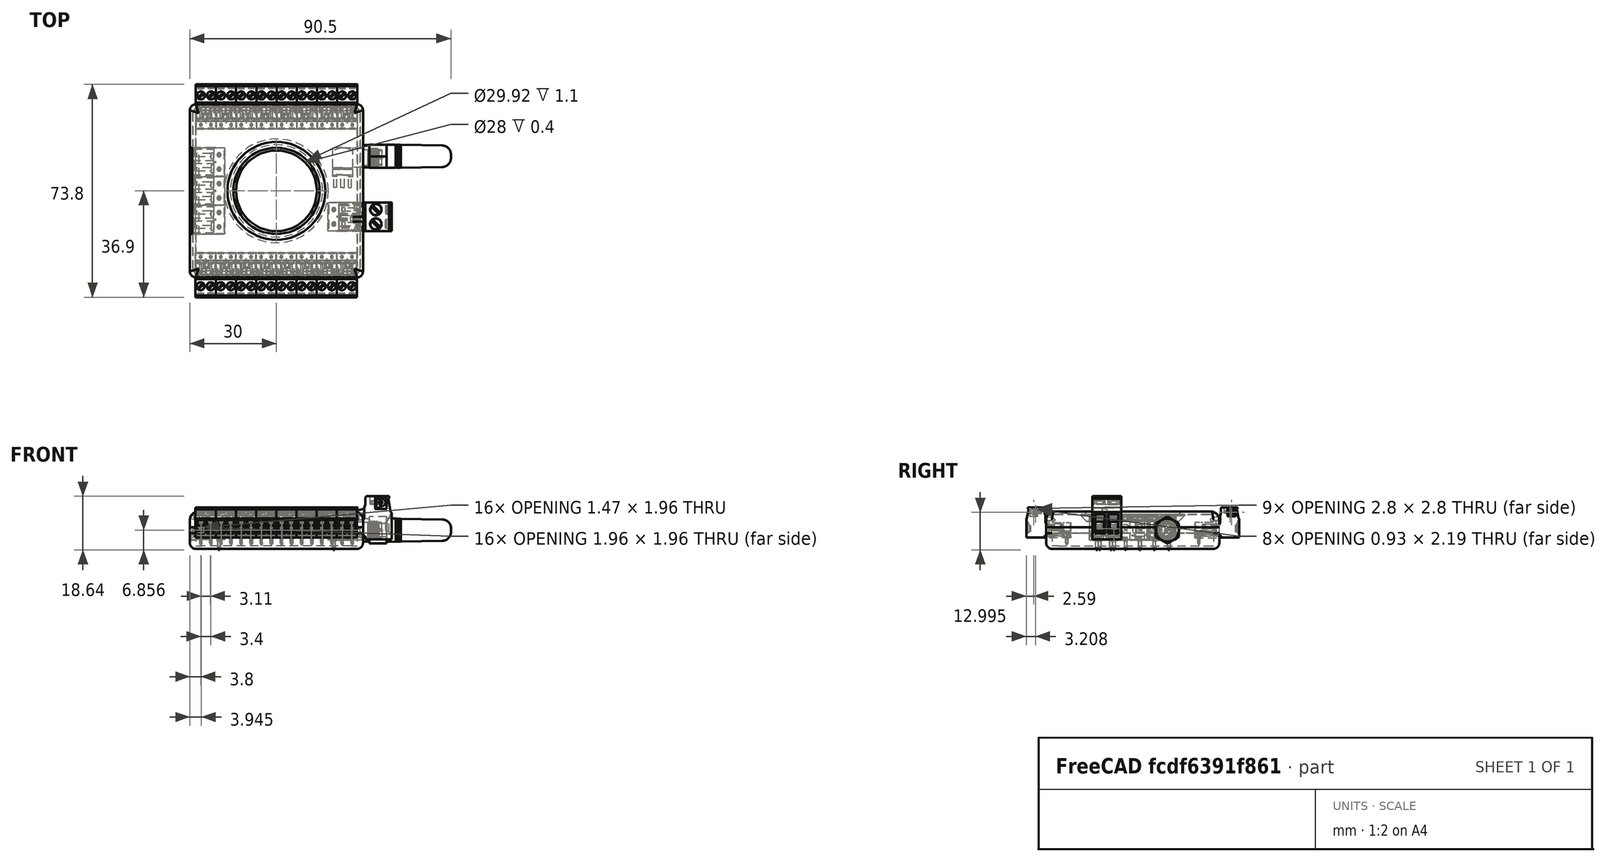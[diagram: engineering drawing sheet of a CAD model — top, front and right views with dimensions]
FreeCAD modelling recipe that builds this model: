
FCSTD DOCUMENT  (FreeCAD 0.16R6704 (Git))
Label: assembly
License: All rights reserved
LicenseURL: http://en.wikipedia.org/wiki/All_rights_reserved
objects: Raytracing::RayFeature×26, Part::FeaturePython×18, Part::Feature×12, Part::Cut×2, Part::Box×1, Raytracing::RayProject×1
note: 33 computed .brp shape members not serialized (recipe doc carries the construction recipe); baked Part::Feature solids carry a one-line shape summary decoded from their .brp

FEATURE [Part::Feature] bottom
  shape: bbox 60 x 60 x 7.5 mm, 48 faces (baked)
FEATURE [Part::Feature] MSTB_2_5_2_ST_1754449___MSTB_2_5__2_G_1754436__Phoenix_Contact_
  Placement = pos=(30,-14,-1) rot=(1,0,0;1.5708rad)
  shape: bbox 18.2 x 10 x 15 mm, 164 faces (baked)
FEATURE [Part::Feature] MSTB_2_5_2_ST_1754449___MSTB_2_5__2_G_1754436__Phoenix_Contact_001
  Placement = pos=(30,-14,-1) rot=(1,0,0;1.5708rad)
  shape: bbox 12.01 x 10.01 x 12.11 mm, 146 faces (baked)
FEATURE [Part::Feature] MSTB_2_5_2_ST_1754449___MSTB_2_5__2_G_1754436__Phoenix_Contact_002
  Placement = pos=(16,-30,-1) rot=(0.57735,-0.57735,-0.57735;2.0944rad)
  shape: bbox 10 x 18.2 x 15 mm, 164 faces (baked)
FEATURE [Part::Feature] MSTB_2_5_2_ST_1754449___MSTB_2_5__2_G_1754436__Phoenix_Contact_003
  Placement = pos=(16,-30,-1) rot=(0.57735,-0.57735,-0.57735;2.0944rad)
  shape: bbox 10.01 x 12.01 x 12.11 mm, 146 faces (baked)
FEATURE [Part::FeaturePython] Scale  # Draft clone (typed FeaturePython)
  Objects = -> [MSTB_2_5_2_ST_1754449___MSTB_2_5__2_G_1754436__Phoenix_Contact_002,MSTB_2_5_2_ST_1754449___MSTB_2_5__2_G_1754436__Phoenix_Contact_003]
  Placement = pos=(9.74983,-8.97,-0.0550038) rot=(0,0,1;0rad)
  Scale = (0.7,0.7,0.7)
FEATURE [Part::FeaturePython] Scale001  # Draft clone (typed FeaturePython)
  Objects = -> [MSTB_2_5_2_ST_1754449___MSTB_2_5__2_G_1754436__Phoenix_Contact_002,MSTB_2_5_2_ST_1754449___MSTB_2_5__2_G_1754436__Phoenix_Contact_003]
  Placement = pos=(2.74983,-8.97,-0.0550038) rot=(0,0,1;0rad)
  Scale = (0.7,0.7,0.7)
FEATURE [Part::FeaturePython] Scale002  # Draft clone (typed FeaturePython)
  Objects = -> [MSTB_2_5_2_ST_1754449___MSTB_2_5__2_G_1754436__Phoenix_Contact_002,MSTB_2_5_2_ST_1754449___MSTB_2_5__2_G_1754436__Phoenix_Contact_003]
  Placement = pos=(-4.25017,-8.97,-0.0550038) rot=(0,0,1;0rad)
  Scale = (0.7,0.7,0.7)
FEATURE [Part::FeaturePython] Scale003  # Draft clone (typed FeaturePython)
  Objects = -> [MSTB_2_5_2_ST_1754449___MSTB_2_5__2_G_1754436__Phoenix_Contact_002,MSTB_2_5_2_ST_1754449___MSTB_2_5__2_G_1754436__Phoenix_Contact_003]
  Placement = pos=(-11.2502,-8.97,-0.0550038) rot=(0,0,1;0rad)
  Scale = (0.7,0.7,0.7)
FEATURE [Part::FeaturePython] Scale004  # Draft clone (typed FeaturePython)
  Objects = -> [MSTB_2_5_2_ST_1754449___MSTB_2_5__2_G_1754436__Phoenix_Contact_002,MSTB_2_5_2_ST_1754449___MSTB_2_5__2_G_1754436__Phoenix_Contact_003]
  Placement = pos=(-18.2502,-8.97,-0.0550038) rot=(0,0,1;0rad)
  Scale = (0.7,0.7,0.7)
FEATURE [Part::FeaturePython] Scale005  # Draft clone (typed FeaturePython)
  Objects = -> [MSTB_2_5_2_ST_1754449___MSTB_2_5__2_G_1754436__Phoenix_Contact_002,MSTB_2_5_2_ST_1754449___MSTB_2_5__2_G_1754436__Phoenix_Contact_003]
  Placement = pos=(-25.2502,-8.97,-0.0550038) rot=(0,0,1;0rad)
  Scale = (0.7,0.7,0.7)
FEATURE [Part::FeaturePython] Scale006  # Draft clone (typed FeaturePython)
  Objects = -> [MSTB_2_5_2_ST_1754449___MSTB_2_5__2_G_1754436__Phoenix_Contact_002,MSTB_2_5_2_ST_1754449___MSTB_2_5__2_G_1754436__Phoenix_Contact_003]
  Placement = pos=(-39.2502,-8.97,-0.0550038) rot=(0,0,1;0rad)
  Scale = (0.7,0.7,0.7)
FEATURE [Part::FeaturePython] Scale007  # Draft clone (typed FeaturePython)
  Objects = -> [MSTB_2_5_2_ST_1754449___MSTB_2_5__2_G_1754436__Phoenix_Contact_002,MSTB_2_5_2_ST_1754449___MSTB_2_5__2_G_1754436__Phoenix_Contact_003]
  Placement = pos=(-32.2502,-8.97,-0.0550038) rot=(0,0,1;0rad)
  Scale = (0.7,0.7,0.7)
FEATURE [Part::FeaturePython] Scale008  # Draft clone (typed FeaturePython)
  Objects = -> [MSTB_2_5_2_ST_1754449___MSTB_2_5__2_G_1754436__Phoenix_Contact_002,MSTB_2_5_2_ST_1754449___MSTB_2_5__2_G_1754436__Phoenix_Contact_003]
  Placement = pos=(-9.74983,8.97,-0.0550038) rot=(0,0,1;3.14159rad)
  Scale = (0.7,0.7,0.7)
FEATURE [Part::FeaturePython] Scale009  # Draft clone (typed FeaturePython)
  Objects = -> [MSTB_2_5_2_ST_1754449___MSTB_2_5__2_G_1754436__Phoenix_Contact_002,MSTB_2_5_2_ST_1754449___MSTB_2_5__2_G_1754436__Phoenix_Contact_003]
  Placement = pos=(-2.74983,8.97,-0.0550038) rot=(0,0,1;3.14159rad)
  Scale = (0.7,0.7,0.7)
FEATURE [Part::FeaturePython] Scale010  # Draft clone (typed FeaturePython)
  Objects = -> [MSTB_2_5_2_ST_1754449___MSTB_2_5__2_G_1754436__Phoenix_Contact_002,MSTB_2_5_2_ST_1754449___MSTB_2_5__2_G_1754436__Phoenix_Contact_003]
  Placement = pos=(4.25017,8.97,-0.0550038) rot=(0,0,1;3.14159rad)
  Scale = (0.7,0.7,0.7)
FEATURE [Part::FeaturePython] Scale011  # Draft clone (typed FeaturePython)
  Objects = -> [MSTB_2_5_2_ST_1754449___MSTB_2_5__2_G_1754436__Phoenix_Contact_002,MSTB_2_5_2_ST_1754449___MSTB_2_5__2_G_1754436__Phoenix_Contact_003]
  Placement = pos=(11.2502,8.97,-0.0550038) rot=(0,0,1;3.14159rad)
  Scale = (0.7,0.7,0.7)
FEATURE [Part::FeaturePython] Scale012  # Draft clone (typed FeaturePython)
  Objects = -> [MSTB_2_5_2_ST_1754449___MSTB_2_5__2_G_1754436__Phoenix_Contact_002,MSTB_2_5_2_ST_1754449___MSTB_2_5__2_G_1754436__Phoenix_Contact_003]
  Placement = pos=(18.2502,8.97,-0.0550038) rot=(0,0,1;3.14159rad)
  Scale = (0.7,0.7,0.7)
FEATURE [Part::FeaturePython] Scale013  # Draft clone (typed FeaturePython)
  Objects = -> [MSTB_2_5_2_ST_1754449___MSTB_2_5__2_G_1754436__Phoenix_Contact_002,MSTB_2_5_2_ST_1754449___MSTB_2_5__2_G_1754436__Phoenix_Contact_003]
  Placement = pos=(25.2502,8.97,-0.0550038) rot=(0,0,1;3.14159rad)
  Scale = (0.7,0.7,0.7)
FEATURE [Part::FeaturePython] Scale014  # Draft clone (typed FeaturePython)
  Objects = -> [MSTB_2_5_2_ST_1754449___MSTB_2_5__2_G_1754436__Phoenix_Contact_002,MSTB_2_5_2_ST_1754449___MSTB_2_5__2_G_1754436__Phoenix_Contact_003]
  Placement = pos=(39.2502,8.97,-0.0550038) rot=(0,0,1;3.14159rad)
  Scale = (0.7,0.7,0.7)
FEATURE [Part::FeaturePython] Scale015  # Draft clone (typed FeaturePython)
  Objects = -> [MSTB_2_5_2_ST_1754449___MSTB_2_5__2_G_1754436__Phoenix_Contact_002,MSTB_2_5_2_ST_1754449___MSTB_2_5__2_G_1754436__Phoenix_Contact_003]
  Placement = pos=(32.2502,8.97,-0.0550038) rot=(0,0,1;3.14159rad)
  Scale = (0.7,0.7,0.7)
FEATURE [Part::Feature] MSTB_2_5_2_ST_1754449___MSTB_2_5__2_G_1754436__Phoenix_Contact_004
  Placement = pos=(-30,15,-1) rot=(0,0.707107,0.707107;3.14159rad)
  shape: bbox 12.01 x 10.01 x 12.11 mm, 146 faces (baked)
FEATURE [Part::Feature] MSTB_2_5_2_ST_1754449___MSTB_2_5__2_G_1754436__Phoenix_Contact_005
  Placement = pos=(-30,5,-1) rot=(0,0.707107,0.707107;3.14159rad)
  shape: bbox 12.01 x 10.01 x 12.11 mm, 146 faces (baked)
FEATURE [Part::Feature] MSTB_2_5_2_ST_1754449___MSTB_2_5__2_G_1754436__Phoenix_Contact_006
  Placement = pos=(-30,-5,-1) rot=(0,0.707107,0.707107;3.14159rad)
  shape: bbox 12.01 x 10.01 x 12.11 mm, 146 faces (baked)
FEATURE [Part::Feature] RP_SMA_Connector
  Placement = pos=(23,15,1) rot=(0.57735,0.57735,-0.57735;2.0944rad)
  shape: bbox 18.75 x 13.9 x 9.901 mm, 96 faces (baked)
FEATURE [Part::Feature] top
  shape: bbox 60 x 60 x 7.5 mm, 43 faces (baked)
FEATURE [Part::Feature] dome
  Placement = pos=(0,0,8) rot=(0,0,1;0rad)
  shape: bbox 29.96 x 29.96 x 5.017 mm, 6 faces, 0 solids (baked)
FEATURE [Part::Feature] _______________SAT_G01R
  Placement = pos=(30,12,1) rot=(0,0,1;4.71239rad)
  shape: bbox 30.5 x 8.1 x 9.238 mm, 48 faces (baked)
FEATURE [Part::Box] Box  label="Cube"
  Height = 10
  Length = 10
  Placement = pos=(-31.726,4.50305,0) rot=(0,0,1;0rad)
  Width = 10
FEATURE [Part::FeaturePython] Scale016  # Draft clone (typed FeaturePython)
  Objects = -> [Box]
  Placement = pos=(-30.8339,-24.033,-2.5) rot=(0,0,1;0rad)
  Scale = (1,3,0.9)
FEATURE [Part::FeaturePython] Scale017  # Draft clone (typed FeaturePython)
  Objects = -> [Box]
  Placement = pos=(-30.8339,-24.033,-2.5) rot=(0,0,1;0rad)
  Scale = (1,3,0.9)
FEATURE [Part::Cut] Cut
  Base = -> top
  Tool = -> Scale016
FEATURE [Part::Cut] Cut001
  Base = -> bottom
  Tool = -> Scale017
FEATURE [Raytracing::RayFeature] Cut001_View
  Result = <blob: 53440 chars omitted>
  Source = -> Cut001
  Transparency = 0
FEATURE [Raytracing::RayFeature] Cut_View
  Result = <blob: 145246 chars omitted>
  Source = -> Cut
  Transparency = 0
FEATURE [Raytracing::RayFeature] _______________SAT_G01R_View
  Result = <blob: 98757 chars omitted>
  Source = -> _______________SAT_G01R
  Transparency = 0
FEATURE [Raytracing::RayFeature] dome_View
  Result = <blob: 73219 chars omitted>
  Source = -> dome
  Transparency = 0
FEATURE [Raytracing::RayFeature] RP_SMA_Connector_View
  Result = <blob: 385886 chars omitted>
  Source = -> RP_SMA_Connector
  Transparency = 0
FEATURE [Raytracing::RayFeature] MSTB_2_5_2_ST_1754449___MSTB_2_5__2_G_1754436__Phoenix_Contact_006_View
  Result = <blob: 179228 chars omitted>
  Source = -> MSTB_2_5_2_ST_1754449___MSTB_2_5__2_G_1754436__Phoenix_Contact_006
  Transparency = 0
FEATURE [Raytracing::RayFeature] MSTB_2_5_2_ST_1754449___MSTB_2_5__2_G_1754436__Phoenix_Contact_005_View
  Result = <blob: 178067 chars omitted>
  Source = -> MSTB_2_5_2_ST_1754449___MSTB_2_5__2_G_1754436__Phoenix_Contact_005
  Transparency = 0
FEATURE [Raytracing::RayFeature] MSTB_2_5_2_ST_1754449___MSTB_2_5__2_G_1754436__Phoenix_Contact_004_View
  Result = <blob: 189469 chars omitted>
  Source = -> MSTB_2_5_2_ST_1754449___MSTB_2_5__2_G_1754436__Phoenix_Contact_004
  Transparency = 0
FEATURE [Raytracing::RayFeature] Scale015_View
  Result = <blob: 405285 chars omitted>
  Source = -> Scale015
  Transparency = 0
FEATURE [Raytracing::RayFeature] Scale014_View
  Result = <blob: 405269 chars omitted>
  Source = -> Scale014
  Transparency = 0
FEATURE [Raytracing::RayFeature] Scale013_View
  Result = <blob: 404136 chars omitted>
  Source = -> Scale013
  Transparency = 0
FEATURE [Raytracing::RayFeature] Scale012_View
  Result = <blob: 402788 chars omitted>
  Source = -> Scale012
  Transparency = 0
FEATURE [Raytracing::RayFeature] Scale011_View
  Result = <blob: 406344 chars omitted>
  Source = -> Scale011
  Transparency = 0
FEATURE [Raytracing::RayFeature] Scale010_View
  Result = <blob: 409155 chars omitted>
  Source = -> Scale010
  Transparency = 0
FEATURE [Raytracing::RayFeature] Scale009_View
  Result = <blob: 409357 chars omitted>
  Source = -> Scale009
  Transparency = 0
FEATURE [Raytracing::RayFeature] Scale008_View
  Result = <blob: 409320 chars omitted>
  Source = -> Scale008
  Transparency = 0
FEATURE [Raytracing::RayFeature] Scale007_View
  Result = <blob: 406832 chars omitted>
  Source = -> Scale007
  Transparency = 0
FEATURE [Raytracing::RayFeature] Scale006_View
  Result = <blob: 406831 chars omitted>
  Source = -> Scale006
  Transparency = 0
FEATURE [Raytracing::RayFeature] Scale005_View
  Result = <blob: 405668 chars omitted>
  Source = -> Scale005
  Transparency = 0
FEATURE [Raytracing::RayFeature] Scale004_View
  Result = <blob: 404346 chars omitted>
  Source = -> Scale004
  Transparency = 0
FEATURE [Raytracing::RayFeature] Scale003_View
  Result = <blob: 400712 chars omitted>
  Source = -> Scale003
  Transparency = 0
FEATURE [Raytracing::RayFeature] Scale002_View
  Result = <blob: 402590 chars omitted>
  Source = -> Scale002
  Transparency = 0
FEATURE [Raytracing::RayFeature] Scale001_View
  Result = <blob: 402773 chars omitted>
  Source = -> Scale001
  Transparency = 0
FEATURE [Raytracing::RayFeature] Scale_View
  Result = <blob: 400885 chars omitted>
  Source = -> Scale
  Transparency = 0
FEATURE [Raytracing::RayFeature] MSTB_2_5_2_ST_1754449___MSTB_2_5__2_G_1754436__Phoenix_Contact_001_View
  Result = <blob: 175884 chars omitted>
  Source = -> MSTB_2_5_2_ST_1754449___MSTB_2_5__2_G_1754436__Phoenix_Contact_001
  Transparency = 0
FEATURE [Raytracing::RayFeature] MSTB_2_5_2_ST_1754449___MSTB_2_5__2_G_1754436__Phoenix_Contact__View
  Result = <blob: 243784 chars omitted>
  Source = -> MSTB_2_5_2_ST_1754449___MSTB_2_5__2_G_1754436__Phoenix_Contact_
  Transparency = 0
FEATURE [Raytracing::RayProject] PovProject
  Camera = // declares positon and view direction\n\n// Generated by FreeCAD (http://www.freecadweb.org/)\n#declare cam_location =  <-82.1804,103.321,-34.5702>;\n#declare cam_look_at  = <2.4677,-3.28423,8.39891>;\n#declare cam_sky      = <0.719575,0.659274,0.218104>;\n#declare cam_angle    = 45; \ncamera {\n  location  cam_location\n  look_at   cam_look_at\n  sky       cam_sky\n  angle     cam_angle \n  right x*800/600\n}
  Group = -> [Cut001_View,Cut_View,_______________SAT_G01R_View,dome_View,RP_SMA_Connector_View,MSTB_2_5_2_ST_1754449___MSTB_2_5__2_G_1754436__Phoenix_Contact_006_View,MSTB_2_5_2_ST_1754449___MSTB_2_5__2_G_1754436__Phoenix_Contact_005_View,MSTB_2_5_2_ST_1754449___MSTB_2_5__2_G_1754436__Phoenix_Contact_004_View,Scale015_View,Scale014_View,Scale013_View,Scale012_View,Scale011_View,Scale010_View,Scale009_View,+11 more]
